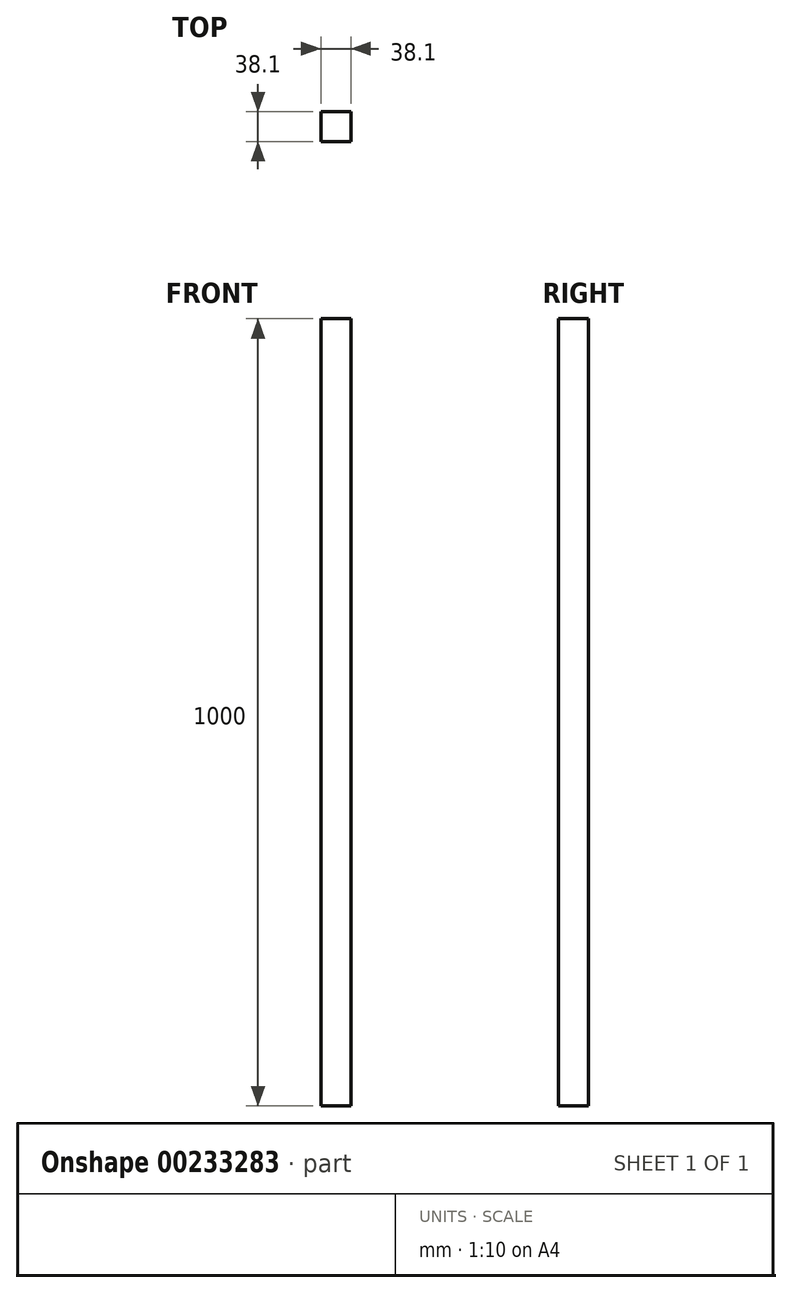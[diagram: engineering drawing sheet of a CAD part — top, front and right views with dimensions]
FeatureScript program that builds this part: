
annotation { "Feature Type Name" : "Feature", "Feature Type Description" : "" }
export const myFeature = defineFeature(function(context is Context, id is Id, definition is map)
    precondition{}
    {
        {
            var Q0;
            Q0=qCreatedBy(makeId("Front.planeOp"),FACE);
            var sketch = newSketch(context, id + "F0", { "sketchPlane" : qUnion([Q0])});
            skLineSegment(sketch, "E0.bottom", {"start": v(-175.61, 547.65) * mm, "end": v(-137.51, 547.65) * mm});
            skLineSegment(sketch, "E0.top", {"start": v(-175.61, -452.35) * mm, "end": v(-137.51, -452.35) * mm});
            skLineSegment(sketch, "E0.left", {"start": v(-175.61, 547.65) * mm, "end": v(-175.61, -452.35) * mm});
            skLineSegment(sketch, "E0.right", {"start": v(-137.51, 547.65) * mm, "end": v(-137.51, -452.35) * mm});
            skSolve(sketch);
        }
        {
            var Q0;
            Q0=makeQuery(id+"F0.imprint","IMPRINT",FACE,{"disambiguationData":[TD([[makeQuery(id+"F0.imprint","IMPRINT",EDGE,{"derivedFrom":sQuery(id+"F0.wireOp",EDGE,"E0.bottom")}),-1.0]])]});
            extrude(context, id + "F1", {"entities" : qUnion([Q0]), "depth" : 38.1 * mm});
        }
    });
